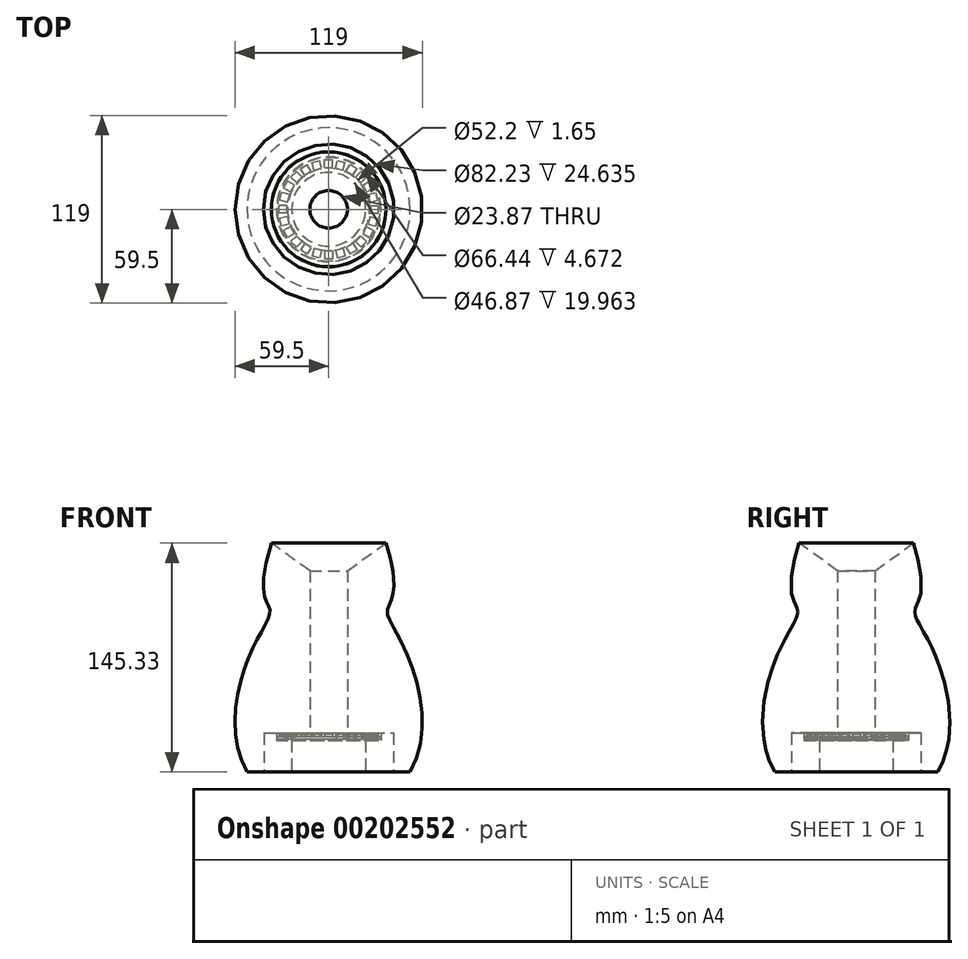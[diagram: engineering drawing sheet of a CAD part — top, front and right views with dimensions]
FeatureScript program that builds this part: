
annotation { "Feature Type Name" : "Feature", "Feature Type Description" : "" }
export const myFeature = defineFeature(function(context is Context, id is Id, definition is map)
    precondition{}
    {
        {
            var Q0;
            Q0=qCreatedBy(makeId("Top.planeOp"),FACE);
            var sketch = newSketch(context, id + "F0", { "sketchPlane" : qUnion([Q0])});
            skCircle(sketch, "E0", {"center": v(0, 0) * mm, "radius": 32.75 * mm});
            skCircle(sketch, "E1", {"center": v(0, 0) * mm, "radius": 26.1 * mm});
            skSolve(sketch);
        }
        {
            var Q0;
            Q0 = qSketchRegion(id + "F0", true);
            extrude(context, id + "F1", {"entities" : qUnion([Q0]), "depth" : 1.65 * mm});
        }
        {
            var Q0;
            Q0=makeQuery(id+"F1.opExtrude","CAP_FACE",FACE,{"disambiguationData":[OSD([sQuery(id+"F0.wireOp",EDGE,"E0"),sQuery(id+"F0.wireOp",EDGE,"E1")])],"isStart":false});
            var sketch = newSketch(context, id + "F2", { "sketchPlane" : qUnion([Q0])});
            skLineSegment(sketch, "E2.bottom", {"start": v(2.5, -26.5) * mm, "end": v(-2.5, -26.5) * mm});
            skLineSegment(sketch, "E2.top", {"start": v(2.5, -31.5) * mm, "end": v(-2.5, -31.5) * mm});
            skLineSegment(sketch, "E2.left", {"start": v(2.5, -26.5) * mm, "end": v(2.5, -31.5) * mm});
            skLineSegment(sketch, "E2.right", {"start": v(-2.5, -26.5) * mm, "end": v(-2.5, -31.5) * mm});
            skPoint(sketch, "E2.middle", {"position": v(0, -29) * mm});
            skSolve(sketch);
        }
        {
            var Q0;
            Q0=makeQuery(id+"F2.imprint","IMPRINT",FACE,{"disambiguationData":[TD([[makeQuery(id+"F2.imprint","IMPRINT",EDGE,{"derivedFrom":sQuery(id+"F2.wireOp",EDGE,"E2.bottom")}),1.0]])]});
            extrude(context, id + "F3", {"entities" : qUnion([Q0]), "depth" : 1.62 * mm});
        }
        {
            var Q0;
            Q0=makeQuery(id+"F3.opExtrude","SWEPT_BODY",BODY,{"disambiguationData":[OSD([sQuery(id+"F2.wireOp",EDGE,"E2.bottom"),sQuery(id+"F2.wireOp",EDGE,"E2.top"),sQuery(id+"F2.wireOp",EDGE,"E2.left"),sQuery(id+"F2.wireOp",EDGE,"E2.right")])]});
            var Q1;
            Q1=makeQuery(id+"F1.opExtrude","CAP_EDGE",EDGE,{"disambiguationData":[OSD([sQuery(id+"F0.wireOp",EDGE,"E0")])],"isStart":false});
            circularPattern(context, id + "F4", {"entities" : qUnion([Q0]), "axis" : qUnion([Q1]), "angle" : 360 * degree, "instanceCount" : 24, "equalSpace" : true});
        }
        {
            var Q0;
            Q0=qCreatedBy(makeId("Front.planeOp"),FACE);
            var sketch = newSketch(context, id + "F5", { "sketchPlane" : qUnion([Q0])});
            skFitSpline(sketch, "E3", {"points": [v(-36.39, 124.73) * mm, v(-37.17, 81.4) * mm, v(-48.9, 56.4) * mm, v(-51.78, -20.6) * mm], "startDerivative": vector(-102.38, -329.73) * mm, "endDerivative": vector(98.67, -168.05) * mm});
            skLineSegment(sketch, "E4", {"start": v(-51.78, -20.6) * mm, "end": v(-23.43, -20.6) * mm});
            skLineSegment(sketch, "E5", {"start": v(-23.43, -20.6) * mm, "end": v(-23.43, -0.64) * mm});
            skLineSegment(sketch, "E6", {"start": v(-23.43, -0.64) * mm, "end": v(-33.22, -0.64) * mm});
            skLineSegment(sketch, "E7", {"start": v(-33.22, -0.64) * mm, "end": v(-33.22, 4.03) * mm});
            skLineSegment(sketch, "E8", {"start": v(-33.22, 4.03) * mm, "end": v(0, 4.03) * mm});
            skLineSegment(sketch, "E9", {"start": v(0, 4.03) * mm, "end": v(0, 98.52) * mm});
            skLineSegment(sketch, "E10", {"start": v(0, 98.52) * mm, "end": v(-36.39, 124.73) * mm});
            skLineSegment(sketch, "E11", {"start": v(-33.22, 4.03) * mm, "end": v(-41.11, 4.03) * mm});
            skLineSegment(sketch, "E12", {"start": v(-41.11, 4.03) * mm, "end": v(-41.11, -20.6) * mm});
            skLineSegment(sketch, "E13", {"start": v(-11.94, 4.03) * mm, "end": v(-11.94, 107.12) * mm});
            skSolve(sketch);
        }
        {
            var Q0;
            {var subQ1=sQuery(id+"F5.wireOp",EDGE,"E3");Q0=makeQuery(id+"F5.imprint","IMPRINT",FACE,{"disambiguationData":[TD([[makeQuery(id+"F5.imprint","IMPRINT",EDGE,{"derivedFrom":subQ1}),1.0]])]});}
            var Q1;
            Q1=sQuery(id+"F5.wireOp",EDGE,"E9");
            revolve(context, id + "F6", {"entities" : qUnion([Q0]), "axis" : qUnion([Q1]), "revolveType" : RevolveType.FULL});
        }
        {
            var Q0;
            {var subQ1=sQuery(id+"F5.wireOp",EDGE,"E5");Q0=makeQuery(id+"F5.imprint","IMPRINT",FACE,{"disambiguationData":[TD([[makeQuery(id+"F5.imprint","IMPRINT",EDGE,{"derivedFrom":subQ1}),1.0]])]});}
            var Q1;
            Q1=sQuery(id+"F5.wireOp",EDGE,"E9");
            revolve(context, id + "F7", {"entities" : qUnion([Q0]), "axis" : qUnion([Q1]), "revolveType" : RevolveType.FULL});
        }
    });
